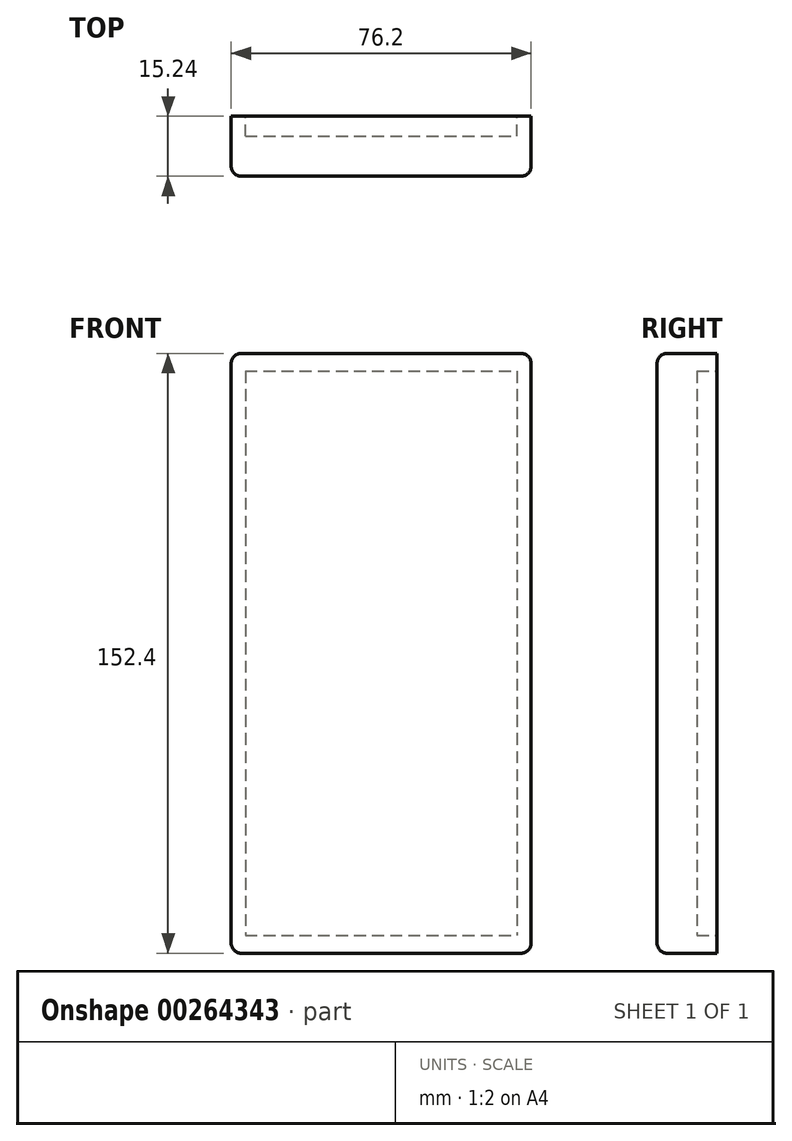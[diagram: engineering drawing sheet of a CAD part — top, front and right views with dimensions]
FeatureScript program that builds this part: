
annotation { "Feature Type Name" : "Feature", "Feature Type Description" : "" }
export const myFeature = defineFeature(function(context is Context, id is Id, definition is map)
    precondition{}
    {
        {
            var Q0;
            Q0=qCreatedBy(makeId("Front.planeOp"),FACE);
            var sketch = newSketch(context, id + "F0", { "sketchPlane" : qUnion([Q0])});
            skLineSegment(sketch, "E0.bottom", {"start": v(-38.1, 76.2) * mm, "end": v(38.1, 76.2) * mm});
            skLineSegment(sketch, "E0.top", {"start": v(-38.1, -76.2) * mm, "end": v(38.1, -76.2) * mm});
            skLineSegment(sketch, "E0.left", {"start": v(-38.1, 76.2) * mm, "end": v(-38.1, -76.2) * mm});
            skLineSegment(sketch, "E0.right", {"start": v(38.1, 76.2) * mm, "end": v(38.1, -76.2) * mm});
            skPoint(sketch, "E0.middle", {"position": v(0, 0) * mm});
            skSolve(sketch);
        }
        {
            var Q0;
            Q0 = qSketchRegion(id + "F0", true);
            extrude(context, id + "F1", {"entities" : qUnion([Q0]), "depth" : 15.24 * mm});
        }
        {
            var Q0;
            Q0=makeQuery(id+"F1.opExtrude","CAP_FACE",FACE,{"disambiguationData":[OSD([sQuery(id+"F0.wireOp",EDGE,"E0.bottom"),sQuery(id+"F0.wireOp",EDGE,"E0.top"),sQuery(id+"F0.wireOp",EDGE,"E0.left"),sQuery(id+"F0.wireOp",EDGE,"E0.right")])],"isStart":true});
            var sketch = newSketch(context, id + "F2", { "sketchPlane" : qUnion([Q0])});
            skLineSegment(sketch, "E1.bottom", {"start": v(34.47, 71.71) * mm, "end": v(-34.47, 71.71) * mm});
            skLineSegment(sketch, "E1.top", {"start": v(34.47, -71.71) * mm, "end": v(-34.47, -71.71) * mm});
            skLineSegment(sketch, "E1.left", {"start": v(34.47, 71.71) * mm, "end": v(34.47, -71.71) * mm});
            skLineSegment(sketch, "E1.right", {"start": v(-34.47, 71.71) * mm, "end": v(-34.47, -71.71) * mm});
            skPoint(sketch, "E1.middle", {"position": v(0, 0) * mm});
            skSolve(sketch);
        }
        {
            var Q0;
            Q0 = qSketchRegion(id + "F2", true);
            extrude(context, id + "F3", {"entities" : qUnion([Q0]), "operationType" : NewBodyOperationType.REMOVE, "oppositeDirection" : true, "depth" : 5.08 * mm});
        }
        {
            var Q0;
            Q0=makeQuery(id+"F1.opExtrude","SWEPT_EDGE",EDGE,{"disambiguationData":[OSD([sQuery(id+"F0.wireOp",EDGE,"E0.top"),sQuery(id+"F0.wireOp",EDGE,"E0.left")])]});
            var Q1;
            Q1=makeQuery(id+"F1.opExtrude","SWEPT_EDGE",EDGE,{"disambiguationData":[OSD([sQuery(id+"F0.wireOp",EDGE,"E0.top"),sQuery(id+"F0.wireOp",EDGE,"E0.right")])]});
            var Q2;
            Q2=makeQuery(id+"F1.opExtrude","SWEPT_EDGE",EDGE,{"disambiguationData":[OSD([sQuery(id+"F0.wireOp",EDGE,"E0.bottom"),sQuery(id+"F0.wireOp",EDGE,"E0.right")])]});
            var Q3;
            Q3=makeQuery(id+"F1.opExtrude","SWEPT_EDGE",EDGE,{"disambiguationData":[OSD([sQuery(id+"F0.wireOp",EDGE,"E0.bottom"),sQuery(id+"F0.wireOp",EDGE,"E0.left")])]});
            var Q4;
            Q4=makeQuery(id+"F1.opExtrude","CAP_EDGE",EDGE,{"disambiguationData":[OSD([sQuery(id+"F0.wireOp",EDGE,"E0.left")])],"isStart":false});
            var Q5;
            Q5=makeQuery(id+"F1.opExtrude","CAP_EDGE",EDGE,{"disambiguationData":[OSD([sQuery(id+"F0.wireOp",EDGE,"E0.right")])],"isStart":false});
            var Q6;
            Q6=makeQuery(id+"F1.opExtrude","CAP_EDGE",EDGE,{"disambiguationData":[OSD([sQuery(id+"F0.wireOp",EDGE,"E0.bottom")])],"isStart":false});
            var Q7;
            Q7=makeQuery(id+"F1.opExtrude","CAP_EDGE",EDGE,{"disambiguationData":[OSD([sQuery(id+"F0.wireOp",EDGE,"E0.top")])],"isStart":false});
            fillet(context, id + "F4", {"entities" : qUnion([Q0, Q1, Q2, Q3, Q4, Q5, Q6, Q7]), "radius" : 2.54 * mm, "tangentPropagation" : true, "allowEdgeOverflow" : false});
        }
    });
